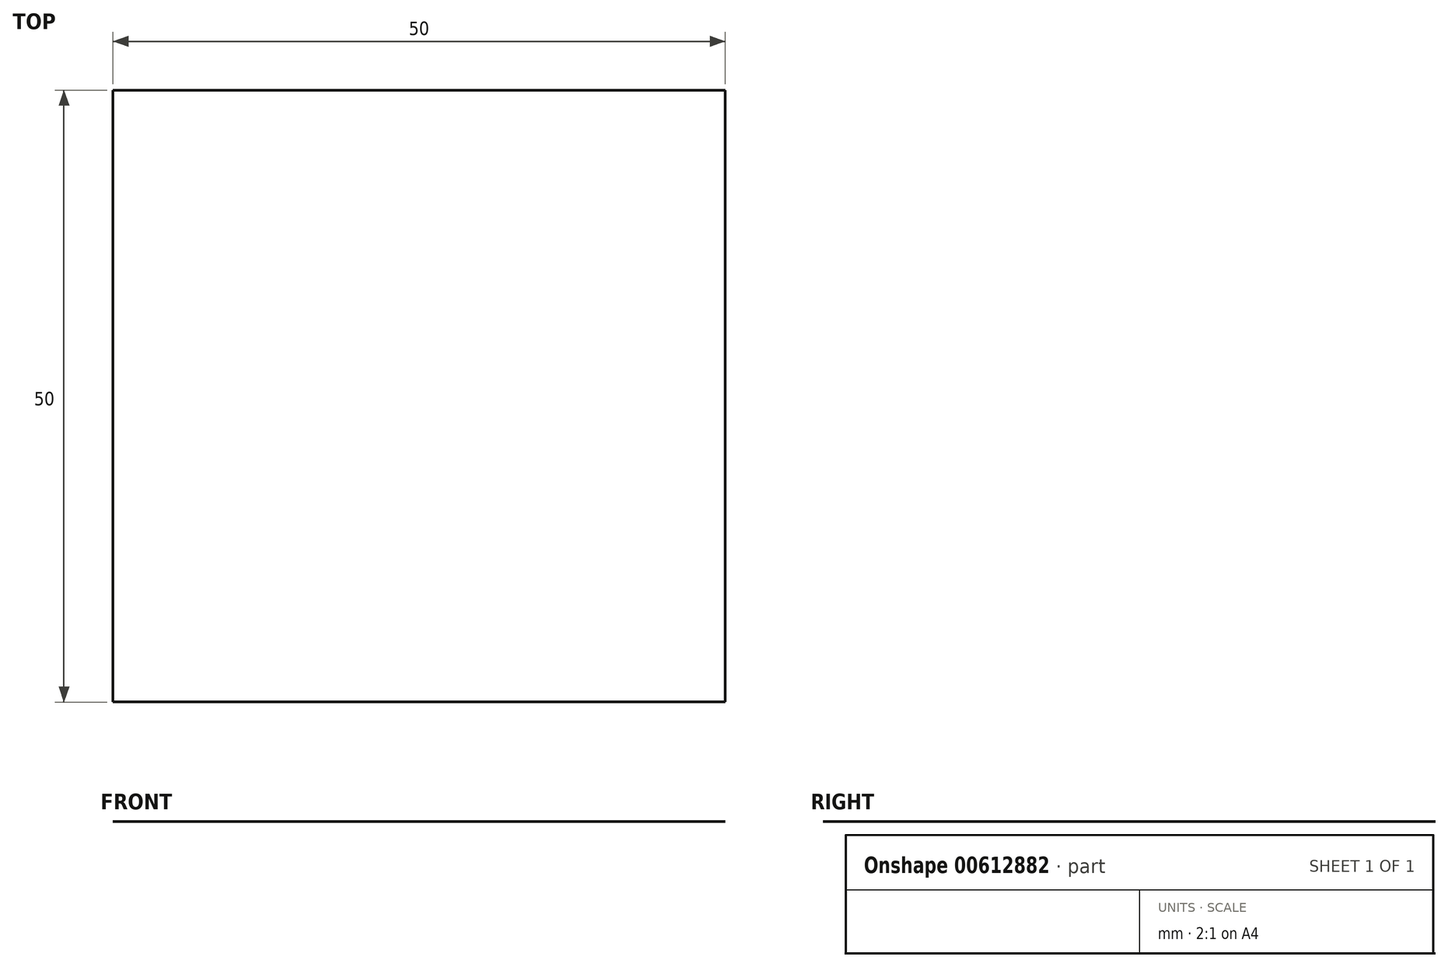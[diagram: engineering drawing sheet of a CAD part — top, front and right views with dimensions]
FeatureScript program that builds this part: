
annotation { "Feature Type Name" : "Feature", "Feature Type Description" : "" }
export const myFeature = defineFeature(function(context is Context, id is Id, definition is map)
    precondition{}
    {
        {
            var Q0;
            Q0=qCreatedBy(makeId("Top.planeOp"),FACE);
            var sketch = newSketch(context, id + "F0", { "sketchPlane" : qUnion([Q0])});
            skLineSegment(sketch, "E0.bottom", {"start": v(-64.96, 58.25) * mm, "end": v(-14.96, 58.25) * mm});
            skLineSegment(sketch, "E0.top", {"start": v(-64.96, 8.25) * mm, "end": v(-14.96, 8.25) * mm});
            skLineSegment(sketch, "E0.left", {"start": v(-64.96, 58.25) * mm, "end": v(-64.96, 8.25) * mm});
            skLineSegment(sketch, "E0.right", {"start": v(-14.96, 58.25) * mm, "end": v(-14.96, 8.25) * mm});
            skSolve(sketch);
        }
        {
            var Q0;
            Q0=makeQuery(id+"F0.imprint","IMPRINT",FACE,{"disambiguationData":[TD([[makeQuery(id+"F0.imprint","IMPRINT",EDGE,{"derivedFrom":sQuery(id+"F0.wireOp",EDGE,"E0.bottom")}),-1.0]])]});
            extrude(context, id + "F1", {"entities" : qUnion([Q0]), "endBound" : BoundingType.SYMMETRIC, "depth" : 0 * mm, "offsetDistance" : 25.4 * mm, "hasDraft" : true, "draftAngle" : 3 * degree});
        }
    });
